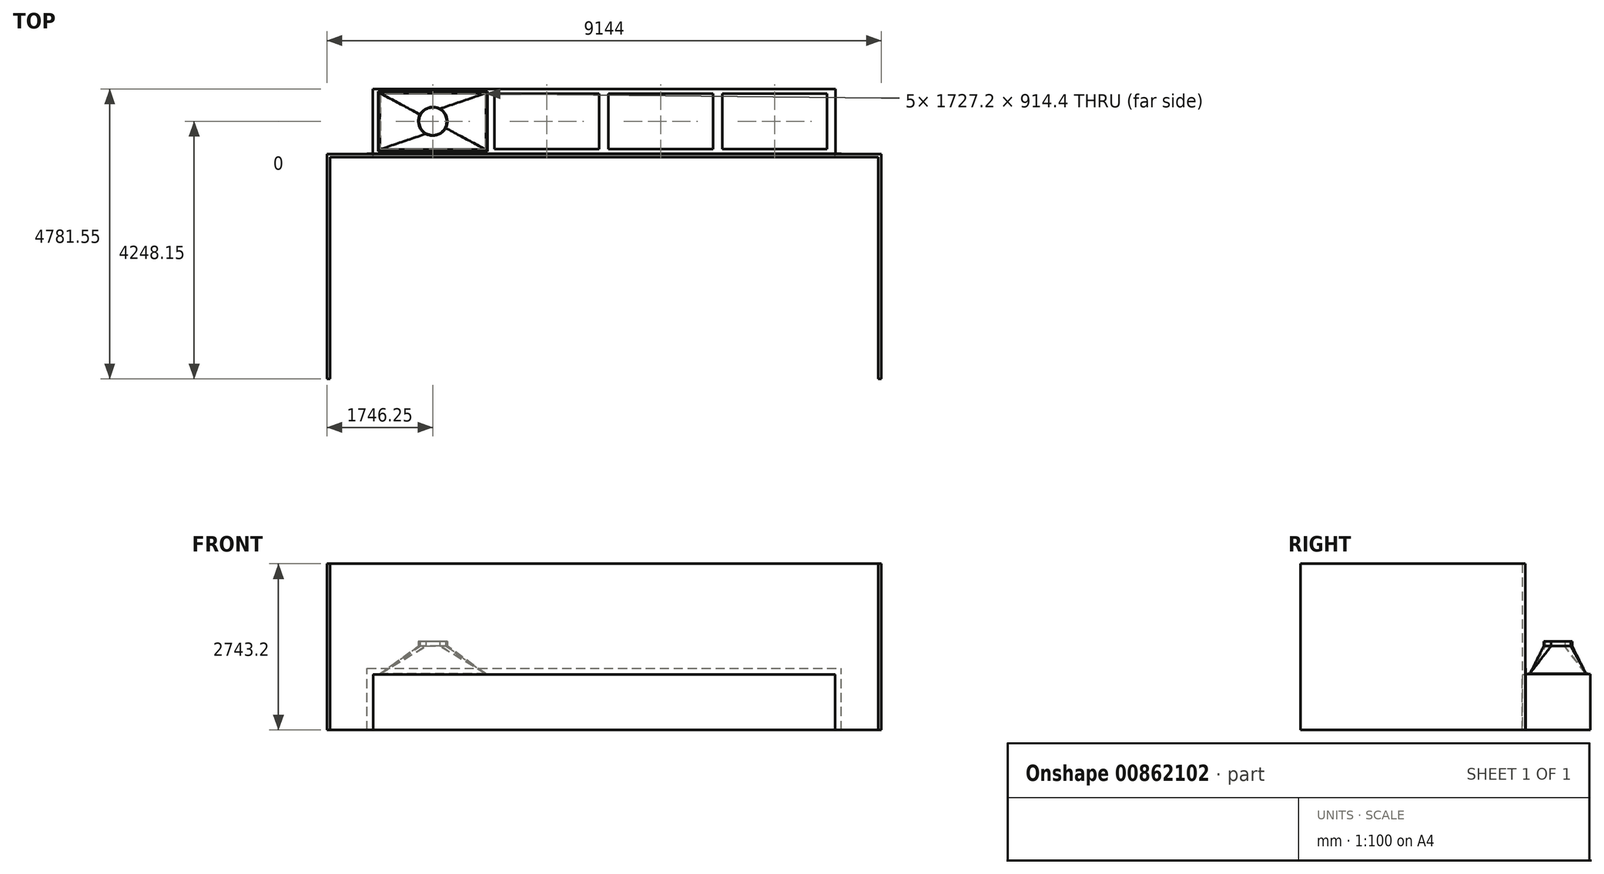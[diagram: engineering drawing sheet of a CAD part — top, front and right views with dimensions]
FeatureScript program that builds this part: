
annotation { "Feature Type Name" : "Feature", "Feature Type Description" : "" }
export const myFeature = defineFeature(function(context is Context, id is Id, definition is map)
    precondition{}
    {
        {
            var Q0;
            Q0=qCreatedBy(makeId("Front.planeOp"),FACE);
            var sketch = newSketch(context, id + "F0", { "sketchPlane" : qUnion([Q0])});
            skLineSegment(sketch, "E0", {"start": v(-3810, 0) * mm, "end": v(3810, 0) * mm, "construction": true});
            skLineSegment(sketch, "E1.top", {"start": v(-3810, 914.4) * mm, "end": v(3810, 914.4) * mm});
            skLineSegment(sketch, "E1.left", {"start": v(-3810, 0) * mm, "end": v(-3810, 914.4) * mm});
            skLineSegment(sketch, "E1.right", {"start": v(3810, 0) * mm, "end": v(3810, 914.4) * mm});
            skLineSegment(sketch, "E2.0", {"start": v(3816.35, 0) * mm, "end": v(3816.35, 920.75) * mm});
            skLineSegment(sketch, "E2.1", {"start": v(-3816.35, 920.75) * mm, "end": v(3816.35, 920.75) * mm});
            skLineSegment(sketch, "E2.2", {"start": v(-3816.35, 0) * mm, "end": v(-3816.35, 920.75) * mm});
            skLineSegment(sketch, "E3", {"start": v(-3816.35, 0) * mm, "end": v(-3810, 0) * mm});
            skLineSegment(sketch, "E4", {"start": v(3810, 0) * mm, "end": v(3816.35, 0) * mm});
            skSolve(sketch);
        }
        {
            var Q0;
            Q0 = qSketchRegion(id + "F0", true);
            extrude(context, id + "F1", {"entities" : qUnion([Q0]), "oppositeDirection" : true, "depth" : 1066.8 * mm, "offsetDistance" : 25.4 * mm});
        }
        {
            var Q0;
            Q0=makeQuery(id+"F1.opExtrude","CAP_FACE",FACE,{"disambiguationData":[OSD([sQuery(id+"F0.wireOp",EDGE,"E1.top"),sQuery(id+"F0.wireOp",EDGE,"E1.left"),sQuery(id+"F0.wireOp",EDGE,"E1.right"),sQuery(id+"F0.wireOp",EDGE,"E2.0"),sQuery(id+"F0.wireOp",EDGE,"E2.1"),sQuery(id+"F0.wireOp",EDGE,"E2.2"),sQuery(id+"F0.wireOp",EDGE,"E3"),sQuery(id+"F0.wireOp",EDGE,"E4")])],"isStart":false});
            var sketch = newSketch(context, id + "F2", { "sketchPlane" : qUnion([Q0])});
            skLineSegment(sketch, "E5.bottom", {"start": v(-3810, 914.4) * mm, "end": v(3810, 914.4) * mm});
            skLineSegment(sketch, "E5.top", {"start": v(-3810, 0) * mm, "end": v(3810, 0) * mm});
            skLineSegment(sketch, "E5.left", {"start": v(-3810, 914.4) * mm, "end": v(-3810, 0) * mm});
            skLineSegment(sketch, "E5.right", {"start": v(3810, 914.4) * mm, "end": v(3810, 0) * mm});
            skSolve(sketch);
        }
        {
            var Q0;
            Q0 = qSketchRegion(id + "F2", true);
            extrude(context, id + "F3", {"entities" : qUnion([Q0]), "operationType" : NewBodyOperationType.ADD, "oppositeDirection" : true, "depth" : 6.35 * mm, "offsetDistance" : 25.4 * mm});
        }
        {
            var Q0;
            Q0=makeQuery(id+"F1.opExtrude","SWEPT_FACE",FACE,{"disambiguationData":[OSD([sQuery(id+"F0.wireOp",EDGE,"E2.1")])]});
            var sketch = newSketch(context, id + "F4", { "sketchPlane" : qUnion([Q0])});
            skLineSegment(sketch, "E6.bottom", {"start": v(-3689.35, 990.6) * mm, "end": v(-1962.15, 990.6) * mm});
            skLineSegment(sketch, "E6.top", {"start": v(-3689.35, 76.2) * mm, "end": v(-1962.15, 76.2) * mm});
            skLineSegment(sketch, "E6.left", {"start": v(-3689.35, 990.6) * mm, "end": v(-3689.35, 76.2) * mm});
            skLineSegment(sketch, "E6.right", {"start": v(-1962.15, 990.6) * mm, "end": v(-1962.15, 76.2) * mm});
            skLineSegment(sketch, "E7.1.0.0", {"start": v(-1809.75, 990.6) * mm, "end": v(-1809.75, 76.2) * mm});
            skLineSegment(sketch, "E7.1.0.1", {"start": v(-1809.75, 990.6) * mm, "end": v(-82.55, 990.6) * mm});
            skLineSegment(sketch, "E7.1.0.2", {"start": v(-82.55, 990.6) * mm, "end": v(-82.55, 76.2) * mm});
            skLineSegment(sketch, "E7.1.0.3", {"start": v(-1809.75, 76.2) * mm, "end": v(-82.55, 76.2) * mm});
            skLineSegment(sketch, "E7.2.0.0", {"start": v(69.85, 990.6) * mm, "end": v(69.85, 76.2) * mm});
            skLineSegment(sketch, "E7.2.0.1", {"start": v(69.85, 990.6) * mm, "end": v(1797.05, 990.6) * mm});
            skLineSegment(sketch, "E7.2.0.2", {"start": v(1797.05, 990.6) * mm, "end": v(1797.05, 76.2) * mm});
            skLineSegment(sketch, "E7.2.0.3", {"start": v(69.85, 76.2) * mm, "end": v(1797.05, 76.2) * mm});
            skLineSegment(sketch, "E7.3.0.0", {"start": v(1949.45, 990.6) * mm, "end": v(1949.45, 76.2) * mm});
            skLineSegment(sketch, "E7.3.0.1", {"start": v(1949.45, 990.6) * mm, "end": v(3676.65, 990.6) * mm});
            skLineSegment(sketch, "E7.3.0.2", {"start": v(3676.65, 990.6) * mm, "end": v(3676.65, 76.2) * mm});
            skLineSegment(sketch, "E7.3.0.3", {"start": v(1949.45, 76.2) * mm, "end": v(3676.65, 76.2) * mm});
            skLineSegment(sketch, "E7.direction1", {"start": v(-3689.35, 76.2) * mm, "end": v(-1809.75, 76.2) * mm, "construction": true});
            skLineSegment(sketch, "E8.bottom", {"start": v(-3816.35, 0) * mm, "end": v(-3689.35, 0) * mm, "construction": true});
            skLineSegment(sketch, "E8.top", {"start": v(-3816.35, 76.2) * mm, "end": v(-3689.35, 76.2) * mm, "construction": true});
            skLineSegment(sketch, "E8.left", {"start": v(-3816.35, 0) * mm, "end": v(-3816.35, 76.2) * mm, "construction": true});
            skLineSegment(sketch, "E8.right", {"start": v(-3689.35, 0) * mm, "end": v(-3689.35, 76.2) * mm, "construction": true});
            skSolve(sketch);
        }
        {
            var Q0;
            Q0 = qSketchRegion(id + "F4", true);
            extrude(context, id + "F5", {"entities" : qUnion([Q0]), "operationType" : NewBodyOperationType.REMOVE, "oppositeDirection" : true, "depth" : 25.4 * mm, "offsetDistance" : 25.4 * mm});
        }
        {
            var Q0;
            Q0=makeQuery(id+"F1.opExtrude","CAP_FACE",FACE,{"disambiguationData":[OSD([sQuery(id+"F0.wireOp",EDGE,"E1.top"),sQuery(id+"F0.wireOp",EDGE,"E1.left"),sQuery(id+"F0.wireOp",EDGE,"E1.right"),sQuery(id+"F0.wireOp",EDGE,"E2.0"),sQuery(id+"F0.wireOp",EDGE,"E2.1"),sQuery(id+"F0.wireOp",EDGE,"E2.2"),sQuery(id+"F0.wireOp",EDGE,"E3"),sQuery(id+"F0.wireOp",EDGE,"E4")])],"isStart":true});
            var sketch = newSketch(context, id + "F6", { "sketchPlane" : qUnion([Q0])});
            skLineSegment(sketch, "E9.0", {"start": v(-3810, 0) * mm, "end": v(-3810, 914.4) * mm});
            skLineSegment(sketch, "E9.1", {"start": v(-3810, 914.4) * mm, "end": v(3810, 914.4) * mm});
            skLineSegment(sketch, "E9.2", {"start": v(3810, 0) * mm, "end": v(3810, 914.4) * mm});
            skLineSegment(sketch, "E10.0", {"start": v(3911.6, 0) * mm, "end": v(3911.6, 1016) * mm});
            skLineSegment(sketch, "E10.1", {"start": v(-3911.6, 1016) * mm, "end": v(3911.6, 1016) * mm});
            skLineSegment(sketch, "E10.2", {"start": v(-3911.6, 0) * mm, "end": v(-3911.6, 1016) * mm});
            skLineSegment(sketch, "E11", {"start": v(-3911.6, 0) * mm, "end": v(-3810, 0) * mm});
            skLineSegment(sketch, "E12", {"start": v(3911.6, 0) * mm, "end": v(3810, 0) * mm});
            skSolve(sketch);
        }
        {
            var Q0;
            Q0 = qSketchRegion(id + "F6", true);
            extrude(context, id + "F7", {"entities" : qUnion([Q0]), "depth" : 6.35 * mm, "offsetDistance" : 25.4 * mm});
        }
        {
            var Q0;
            Q0=makeQuery(id+"F1.opExtrude","SWEPT_FACE",FACE,{"disambiguationData":[OSD([sQuery(id+"F0.wireOp",EDGE,"E2.1")])]});
            var sketch = newSketch(context, id + "F8", { "sketchPlane" : qUnion([Q0])});
            skLineSegment(sketch, "E13.0", {"start": v(-3689.35, 990.6) * mm, "end": v(-3689.35, 76.2) * mm});
            skLineSegment(sketch, "E13.1", {"start": v(-3689.35, 76.2) * mm, "end": v(-1962.15, 76.2) * mm});
            skLineSegment(sketch, "E13.2", {"start": v(-1962.15, 990.6) * mm, "end": v(-1962.15, 76.2) * mm});
            skLineSegment(sketch, "E13.3", {"start": v(-3689.35, 990.6) * mm, "end": v(-1962.15, 990.6) * mm});
            skLineSegment(sketch, "E14.0", {"start": v(-3727.45, 38.1) * mm, "end": v(-1924.05, 38.1) * mm});
            skLineSegment(sketch, "E14.1", {"start": v(-3727.45, 1028.7) * mm, "end": v(-3727.45, 38.1) * mm});
            skLineSegment(sketch, "E14.2", {"start": v(-3727.45, 1028.7) * mm, "end": v(-1924.05, 1028.7) * mm});
            skLineSegment(sketch, "E14.3", {"start": v(-1924.05, 1028.7) * mm, "end": v(-1924.05, 38.1) * mm});
            skSolve(sketch);
        }
        {
            var Q0;
            Q0 = qSketchRegion(id + "F8", true);
            extrude(context, id + "F9", {"entities" : qUnion([Q0]), "depth" : 6.35 * mm, "offsetDistance" : 25.4 * mm});
        }
        {
            var Q0;
            Q0=makeQuery(id+"F9.opExtrude","CAP_FACE",FACE,{"disambiguationData":[OSD([sQuery(id+"F8.wireOp",EDGE,"E13.0"),sQuery(id+"F8.wireOp",EDGE,"E13.1"),sQuery(id+"F8.wireOp",EDGE,"E13.2"),sQuery(id+"F8.wireOp",EDGE,"E13.3"),sQuery(id+"F8.wireOp",EDGE,"E14.0"),sQuery(id+"F8.wireOp",EDGE,"E14.1"),sQuery(id+"F8.wireOp",EDGE,"E14.2"),sQuery(id+"F8.wireOp",EDGE,"E14.3")])],"isStart":false});
            cPlane(context, id + "F10", {"entities" : qUnion([Q0]), "cplaneType" : CPlaneType.OFFSET, "offset" : 457.2 * mm, "width" : 152.4 * mm, "height" : 152.4 * mm});
        }
        {
            var Q0;
            Q0=makeQuery(id+"F9.opExtrude","CAP_FACE",FACE,{"disambiguationData":[OSD([sQuery(id+"F8.wireOp",EDGE,"E13.0"),sQuery(id+"F8.wireOp",EDGE,"E13.1"),sQuery(id+"F8.wireOp",EDGE,"E13.2"),sQuery(id+"F8.wireOp",EDGE,"E13.3"),sQuery(id+"F8.wireOp",EDGE,"E14.0"),sQuery(id+"F8.wireOp",EDGE,"E14.1"),sQuery(id+"F8.wireOp",EDGE,"E14.2"),sQuery(id+"F8.wireOp",EDGE,"E14.3")])],"isStart":false});
            var sketch = newSketch(context, id + "F11", { "sketchPlane" : qUnion([Q0])});
            skLineSegment(sketch, "E15", {"start": v(-3689.35, 533.4) * mm, "end": v(-2825.75, 533.4) * mm, "construction": true});
            skPoint(sketch, "E15.endSnap0", {"position": v(-2825.75, 990.6) * mm});
            skLineSegment(sketch, "E16", {"start": v(-2825.75, 533.4) * mm, "end": v(-2825.75, 990.6) * mm, "construction": true});
            skLineSegment(sketch, "E17.bottom", {"start": v(-3689.35, 76.2) * mm, "end": v(-1962.15, 76.2) * mm});
            skLineSegment(sketch, "E17.top", {"start": v(-3689.35, 990.6) * mm, "end": v(-1962.15, 990.6) * mm});
            skLineSegment(sketch, "E17.left", {"start": v(-3689.35, 76.2) * mm, "end": v(-3689.35, 990.6) * mm});
            skLineSegment(sketch, "E17.right", {"start": v(-1962.15, 76.2) * mm, "end": v(-1962.15, 990.6) * mm});
            skSolve(sketch);
        }
        {
            var Q0;
            Q0=qCreatedBy(id+"F10.planeOp",FACE);
            var sketch = newSketch(context, id + "F12", { "sketchPlane" : qUnion([Q0])});
            skCircle(sketch, "E18", {"center": v(-2825.75, 533.4) * mm, "radius": 228.6 * mm});
            skSolve(sketch);
        }
        {
            var Q1;
            Q1 = qSketchRegion(id + "F11", true);
            var Q2;
            Q2 = qSketchRegion(id + "F12", true);
            loft(context, id + "F13", {"sheetProfilesArray" : [{ "sheetProfileEntities" : qUnion([Q1]) }, { "sheetProfileEntities" : qUnion([Q2]) }]});
        }
        {
            var Q0;
            Q0=makeQuery(id+"F13.opLoft","CAP_FACE",FACE,{"disambiguationData":[OSD([makeQuery(id+"F12.imprint","IMPRINT",FACE,{"disambiguationData":[TD([[makeQuery(id+"F12.imprint","IMPRINT",EDGE,{"derivedFrom":sQuery(id+"F12.wireOp",EDGE,"E18")}),1.0]])]})])],"isStart":true});
            var Q1;
            Q1=makeQuery(id+"F13.opLoft","CAP_FACE",FACE,{"disambiguationData":[OSD([makeQuery(id+"F11.imprint","IMPRINT",FACE,{"disambiguationData":[TD([[makeQuery(id+"F11.imprint","IMPRINT",EDGE,{"derivedFrom":sQuery(id+"F11.wireOp",EDGE,"E17.bottom")}),1.0]])]})])],"isStart":true});
            shell(context, id + "F14", {"entities" : qUnion([Q0, Q1]), "thickness" : 6.35 * mm, "oppositeDirection" : true});
        }
        {
            var Q0;
            Q0=makeQuery(id+"F13.opLoft","CAP_FACE",FACE,{"disambiguationData":[OSD([makeQuery(id+"F12.imprint","IMPRINT",FACE,{"disambiguationData":[TD([[makeQuery(id+"F12.imprint","IMPRINT",EDGE,{"derivedFrom":sQuery(id+"F12.wireOp",EDGE,"E18")}),1.0]])]})])],"isStart":true});
            extrude(context, id + "F15", {"entities" : qUnion([Q0]), "operationType" : NewBodyOperationType.ADD, "depth" : 76.2 * mm, "offsetDistance" : 25.4 * mm});
        }
        {
            var Q0;
            Q0=makeQuery(id+"F7.opExtrude","CAP_FACE",FACE,{"disambiguationData":[OSD([sQuery(id+"F6.wireOp",EDGE,"E9.0"),sQuery(id+"F6.wireOp",EDGE,"E9.1"),sQuery(id+"F6.wireOp",EDGE,"E9.2"),sQuery(id+"F6.wireOp",EDGE,"E10.0"),sQuery(id+"F6.wireOp",EDGE,"E10.1"),sQuery(id+"F6.wireOp",EDGE,"E10.2"),sQuery(id+"F6.wireOp",EDGE,"E11"),sQuery(id+"F6.wireOp",EDGE,"E12")])],"isStart":false});
            var sketch = newSketch(context, id + "F16", { "sketchPlane" : qUnion([Q0])});
            skLineSegment(sketch, "E19.0", {"start": v(-3810, 0) * mm, "end": v(-3810, 914.4) * mm});
            skLineSegment(sketch, "E19.1", {"start": v(-3810, 914.4) * mm, "end": v(3810, 914.4) * mm});
            skLineSegment(sketch, "E19.2", {"start": v(3810, 0) * mm, "end": v(3810, 914.4) * mm});
            skLineSegment(sketch, "E20.0", {"start": v(4572, 0) * mm, "end": v(4572, 2743.2) * mm});
            skLineSegment(sketch, "E20.1", {"start": v(-4572, 2743.2) * mm, "end": v(4572, 2743.2) * mm});
            skLineSegment(sketch, "E20.2", {"start": v(-4572, 0) * mm, "end": v(-4572, 2743.2) * mm});
            skLineSegment(sketch, "E21", {"start": v(0, 914.4) * mm, "end": v(0, 2743.2) * mm, "construction": true});
            skLineSegment(sketch, "E22", {"start": v(-4572, 0) * mm, "end": v(-3810, 0) * mm});
            skLineSegment(sketch, "E23", {"start": v(3810, 0) * mm, "end": v(4572, 0) * mm});
            skSolve(sketch);
        }
        {
            var Q0;
            Q0 = qSketchRegion(id + "F16", true);
            extrude(context, id + "F17", {"entities" : qUnion([Q0]), "depth" : 50.8 * mm, "offsetDistance" : 25.4 * mm});
        }
        {
            var Q0;
            Q0=makeQuery(id+"F17.opExtrude","CAP_FACE",FACE,{"disambiguationData":[OSD([sQuery(id+"F16.wireOp",EDGE,"E19.0"),sQuery(id+"F16.wireOp",EDGE,"E19.1"),sQuery(id+"F16.wireOp",EDGE,"E19.2"),sQuery(id+"F16.wireOp",EDGE,"E20.0"),sQuery(id+"F16.wireOp",EDGE,"E20.1"),sQuery(id+"F16.wireOp",EDGE,"E20.2"),sQuery(id+"F16.wireOp",EDGE,"E22"),sQuery(id+"F16.wireOp",EDGE,"E23")])],"isStart":false});
            var sketch = newSketch(context, id + "F18", { "sketchPlane" : qUnion([Q0])});
            skLineSegment(sketch, "E24.bottom", {"start": v(-4572, 2743.2) * mm, "end": v(-4521.2, 2743.2) * mm});
            skLineSegment(sketch, "E24.top", {"start": v(-4572, 0) * mm, "end": v(-4521.2, 0) * mm});
            skLineSegment(sketch, "E24.left", {"start": v(-4572, 2743.2) * mm, "end": v(-4572, 0) * mm});
            skLineSegment(sketch, "E24.right", {"start": v(-4521.2, 2743.2) * mm, "end": v(-4521.2, 0) * mm});
            skSolve(sketch);
        }
        {
            var Q0;
            Q0 = qSketchRegion(id + "F18", true);
            extrude(context, id + "F19", {"entities" : qUnion([Q0]), "depth" : 3657.6 * mm, "offsetDistance" : 25.4 * mm});
        }
        {
            var Q0;
            Q0=makeQuery(id+"F19.opExtrude","SWEPT_BODY",BODY,{"disambiguationData":[OSD([sQuery(id+"F18.wireOp",EDGE,"E24.bottom"),sQuery(id+"F18.wireOp",EDGE,"E24.top"),sQuery(id+"F18.wireOp",EDGE,"E24.left"),sQuery(id+"F18.wireOp",EDGE,"E24.right")])]});
            var Q1;
            Q1=qCreatedBy(makeId("Right.planeOp"),FACE);
            mirror(context, id + "F20", {"operationType" : NewBodyOperationType.ADD, "entities" : qUnion([Q0]), "mirrorPlane" : qUnion([Q1])});
        }
    });
